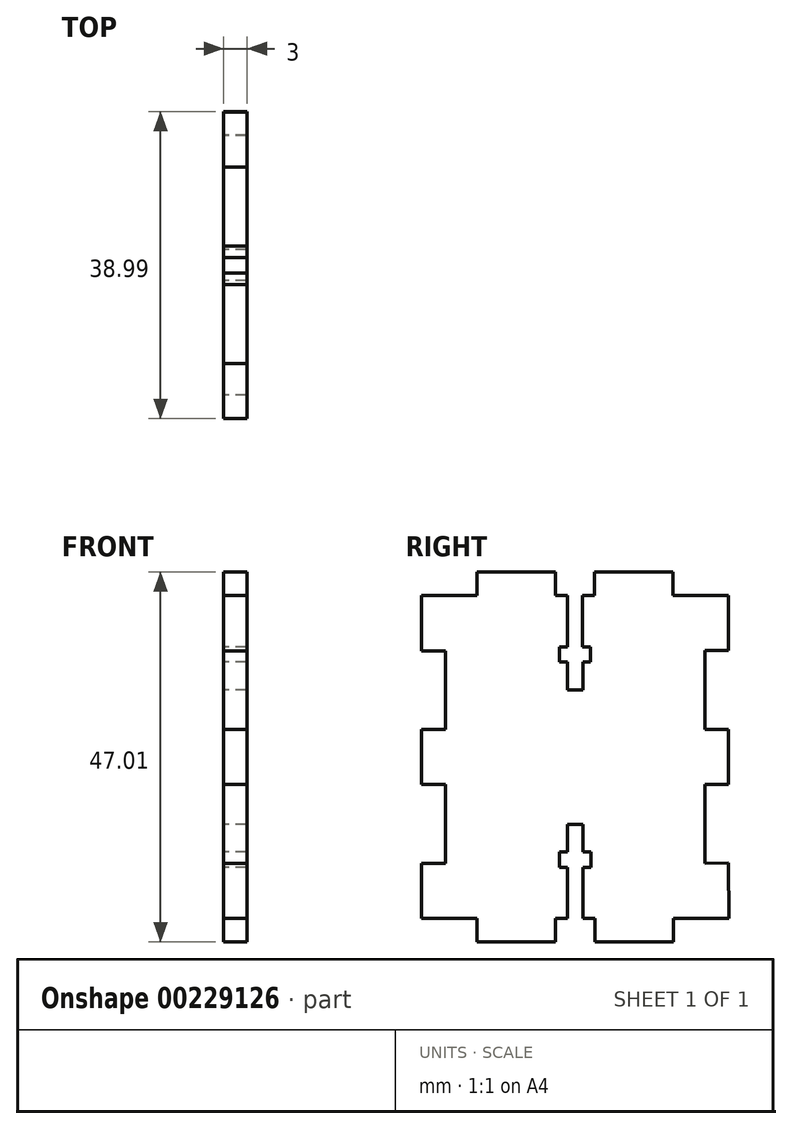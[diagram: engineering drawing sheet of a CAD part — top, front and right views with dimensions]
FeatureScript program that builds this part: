
annotation { "Feature Type Name" : "Feature", "Feature Type Description" : "" }
export const myFeature = defineFeature(function(context is Context, id is Id, definition is map)
    precondition{}
    {
        {
            var Q0;
            Q0=qCreatedBy(makeId("Right.planeOp"),FACE);
            var sketch = newSketch(context, id + "F0", { "sketchPlane" : qUnion([Q0])});
            skLineSegment(sketch, "E0", {"start": v(-19.48, 3.49) * mm, "end": v(-16.48, 3.49) * mm});
            skLineSegment(sketch, "E1", {"start": v(-16.48, 3.49) * mm, "end": v(-16.48, 13.49) * mm});
            skLineSegment(sketch, "E2", {"start": v(-16.48, 13.49) * mm, "end": v(-19.48, 13.49) * mm});
            skLineSegment(sketch, "E3", {"start": v(-19.48, 13.49) * mm, "end": v(-19.48, 20.49) * mm});
            skLineSegment(sketch, "E4", {"start": v(-19.48, 20.49) * mm, "end": v(-12.48, 20.49) * mm});
            skLineSegment(sketch, "E5", {"start": v(-12.48, 20.49) * mm, "end": v(-12.48, 23.49) * mm});
            skLineSegment(sketch, "E6", {"start": v(-12.48, 23.49) * mm, "end": v(-2.48, 23.49) * mm});
            skLineSegment(sketch, "E7", {"start": v(-2.48, 23.49) * mm, "end": v(-2.48, 20.49) * mm});
            skLineSegment(sketch, "E8", {"start": v(-2.48, 20.49) * mm, "end": v(-0.98, 20.49) * mm});
            skLineSegment(sketch, "E9", {"start": v(-0.98, 20.49) * mm, "end": v(-0.98, 13.99) * mm});
            skLineSegment(sketch, "E10", {"start": v(-0.98, 12.04) * mm, "end": v(-0.98, 8.54) * mm});
            skLineSegment(sketch, "E11", {"start": v(-0.98, 8.54) * mm, "end": v(0.02, 8.54) * mm});
            skLineSegment(sketch, "E12", {"start": v(-19.48, -0.01) * mm, "end": v(13.29, -0.01) * mm, "construction": true});
            skPoint(sketch, "E12.endSnap0", {"position": v(-19.48, -0.01) * mm});
            skLineSegment(sketch, "E13", {"start": v(-19.48, 3.49) * mm, "end": v(-19.48, -0.01) * mm});
            skLineSegment(sketch, "E14.MirrorCS", {"start": v(-0.98, -8.57) * mm, "end": v(0.02, -8.57) * mm});
            skLineSegment(sketch, "E15.MirrorCS", {"start": v(-2.48, -20.51) * mm, "end": v(-0.98, -20.51) * mm});
            skLineSegment(sketch, "E16.MirrorCS", {"start": v(-0.98, -12.07) * mm, "end": v(-0.98, -8.57) * mm});
            skLineSegment(sketch, "E17.MirrorCS", {"start": v(-16.48, -3.51) * mm, "end": v(-16.48, -13.51) * mm});
            skLineSegment(sketch, "E18.MirrorCS", {"start": v(-16.48, -13.51) * mm, "end": v(-19.48, -13.51) * mm});
            skLineSegment(sketch, "E19.MirrorCS", {"start": v(-19.48, -20.51) * mm, "end": v(-12.48, -20.51) * mm});
            skLineSegment(sketch, "E20.MirrorCS", {"start": v(-12.48, -20.51) * mm, "end": v(-12.48, -23.51) * mm});
            skLineSegment(sketch, "E21.MirrorCS", {"start": v(-12.48, -23.51) * mm, "end": v(-2.48, -23.51) * mm});
            skLineSegment(sketch, "E22.MirrorCS", {"start": v(-0.98, -20.51) * mm, "end": v(-0.98, -14.01) * mm});
            skLineSegment(sketch, "E23.MirrorCS", {"start": v(-19.48, -13.51) * mm, "end": v(-19.48, -20.51) * mm});
            skLineSegment(sketch, "E24.MirrorCS", {"start": v(-19.48, -3.51) * mm, "end": v(-19.48, -0.01) * mm});
            skLineSegment(sketch, "E25.MirrorCS", {"start": v(-19.48, -3.51) * mm, "end": v(-16.48, -3.51) * mm});
            skLineSegment(sketch, "E26.MirrorCS", {"start": v(-2.48, -23.51) * mm, "end": v(-2.48, -20.51) * mm});
            skLineSegment(sketch, "E27", {"start": v(-0.02, 28.35) * mm, "end": v(0.02, -27.3) * mm, "construction": true});
            skLineSegment(sketch, "E28.MirrorCS", {"start": v(1, -8.57) * mm, "end": v(0, -8.57) * mm});
            skLineSegment(sketch, "E29.MirrorCS", {"start": v(2.51, -23.51) * mm, "end": v(2.5, -20.51) * mm});
            skLineSegment(sketch, "E30.MirrorCS", {"start": v(12.5, -20.5) * mm, "end": v(12.51, -23.5) * mm});
            skLineSegment(sketch, "E31.MirrorCS", {"start": v(16.5, -13.5) * mm, "end": v(19.5, -13.49) * mm});
            skLineSegment(sketch, "E32.MirrorCS", {"start": v(19.49, -3.49) * mm, "end": v(19.48, 0.01) * mm});
            skLineSegment(sketch, "E33.MirrorCS", {"start": v(2.5, -20.51) * mm, "end": v(1, -20.51) * mm});
            skLineSegment(sketch, "E34.MirrorCS", {"start": v(12.46, 20.5) * mm, "end": v(12.45, 23.5) * mm});
            skLineSegment(sketch, "E35.MirrorCS", {"start": v(0.97, 8.54) * mm, "end": v(-0.03, 8.54) * mm});
            skLineSegment(sketch, "E36.MirrorCS", {"start": v(19.49, -3.49) * mm, "end": v(16.49, -3.5) * mm});
            skLineSegment(sketch, "E37.MirrorCS", {"start": v(19.48, 3.51) * mm, "end": v(19.48, 0.01) * mm});
            skLineSegment(sketch, "E38.MirrorCS", {"start": v(19.48, 3.51) * mm, "end": v(16.48, 3.5) * mm});
            skLineSegment(sketch, "E39.MirrorCS", {"start": v(2.45, 23.49) * mm, "end": v(2.46, 20.49) * mm});
            skLineSegment(sketch, "E40.MirrorCS", {"start": v(2.46, 20.49) * mm, "end": v(0.96, 20.49) * mm});
            skLineSegment(sketch, "E41.MirrorCS", {"start": v(16.46, 13.5) * mm, "end": v(19.46, 13.51) * mm});
            skPoint(sketch, "E42.MirrorP", {"position": v(19.48, 0.01) * mm});
            skLineSegment(sketch, "E43.MirrorCS", {"start": v(0.97, 12.04) * mm, "end": v(0.97, 8.54) * mm});
            skLineSegment(sketch, "E44.MirrorCS", {"start": v(1, -20.51) * mm, "end": v(1, -14.01) * mm});
            skLineSegment(sketch, "E45.MirrorCS", {"start": v(19.46, 20.51) * mm, "end": v(12.46, 20.5) * mm});
            skLineSegment(sketch, "E46.MirrorCS", {"start": v(16.49, -3.5) * mm, "end": v(16.5, -13.5) * mm});
            skLineSegment(sketch, "E47.MirrorCS", {"start": v(1, -12.07) * mm, "end": v(1, -8.57) * mm});
            skLineSegment(sketch, "E48.MirrorCS", {"start": v(19.46, 13.51) * mm, "end": v(19.46, 20.51) * mm});
            skLineSegment(sketch, "E49.MirrorCS", {"start": v(12.45, 23.5) * mm, "end": v(2.45, 23.49) * mm});
            skLineSegment(sketch, "E50.MirrorCS", {"start": v(19.48, 0.01) * mm, "end": v(-13.29, -0.03) * mm, "construction": true});
            skLineSegment(sketch, "E51.MirrorCS", {"start": v(16.48, 3.5) * mm, "end": v(16.46, 13.5) * mm});
            skLineSegment(sketch, "E52.MirrorCS", {"start": v(19.5, -20.49) * mm, "end": v(12.5, -20.5) * mm});
            skLineSegment(sketch, "E53.MirrorCS", {"start": v(19.5, -13.49) * mm, "end": v(19.5, -20.49) * mm});
            skLineSegment(sketch, "E54.MirrorCS", {"start": v(0.96, 20.49) * mm, "end": v(0.96, 13.99) * mm});
            skLineSegment(sketch, "E55.MirrorCS", {"start": v(12.51, -23.5) * mm, "end": v(2.51, -23.51) * mm});
            skLineSegment(sketch, "E56", {"start": v(-0.98, 13.99) * mm, "end": v(-1.98, 13.99) * mm});
            skLineSegment(sketch, "E57", {"start": v(-0.98, 12.04) * mm, "end": v(-1.98, 12.04) * mm});
            skLineSegment(sketch, "E58", {"start": v(-1.98, 13.99) * mm, "end": v(-1.98, 12.04) * mm});
            skLineSegment(sketch, "E59", {"start": v(0.97, 12.04) * mm, "end": v(1.96, 12.04) * mm});
            skLineSegment(sketch, "E60", {"start": v(0.96, 13.99) * mm, "end": v(1.96, 13.99) * mm});
            skLineSegment(sketch, "E61", {"start": v(1.96, 13.99) * mm, "end": v(1.96, 12.04) * mm});
            skLineSegment(sketch, "E62", {"start": v(-0.98, -12.07) * mm, "end": v(-1.98, -12.07) * mm});
            skLineSegment(sketch, "E63", {"start": v(1, -12.07) * mm, "end": v(2, -12.07) * mm});
            skLineSegment(sketch, "E64", {"start": v(1, -14.01) * mm, "end": v(2, -14.01) * mm});
            skLineSegment(sketch, "E65", {"start": v(-0.98, -14.01) * mm, "end": v(-1.98, -14.01) * mm});
            skLineSegment(sketch, "E66", {"start": v(-1.98, -12.07) * mm, "end": v(-1.98, -14.01) * mm});
            skLineSegment(sketch, "E67", {"start": v(2, -12.07) * mm, "end": v(2, -14.01) * mm});
            skSolve(sketch);
        }
        {
            var Q0;
            Q0=makeQuery(id+"F0.imprint","IMPRINT",FACE,{"disambiguationData":[TD([[makeQuery(id+"F0.imprint","IMPRINT",EDGE,{"derivedFrom":sQuery(id+"F0.wireOp",EDGE,"E0")}),-1.0]])]});
            extrude(context, id + "F1", {"entities" : qUnion([Q0]), "depth" : 3 * mm});
        }
    });
